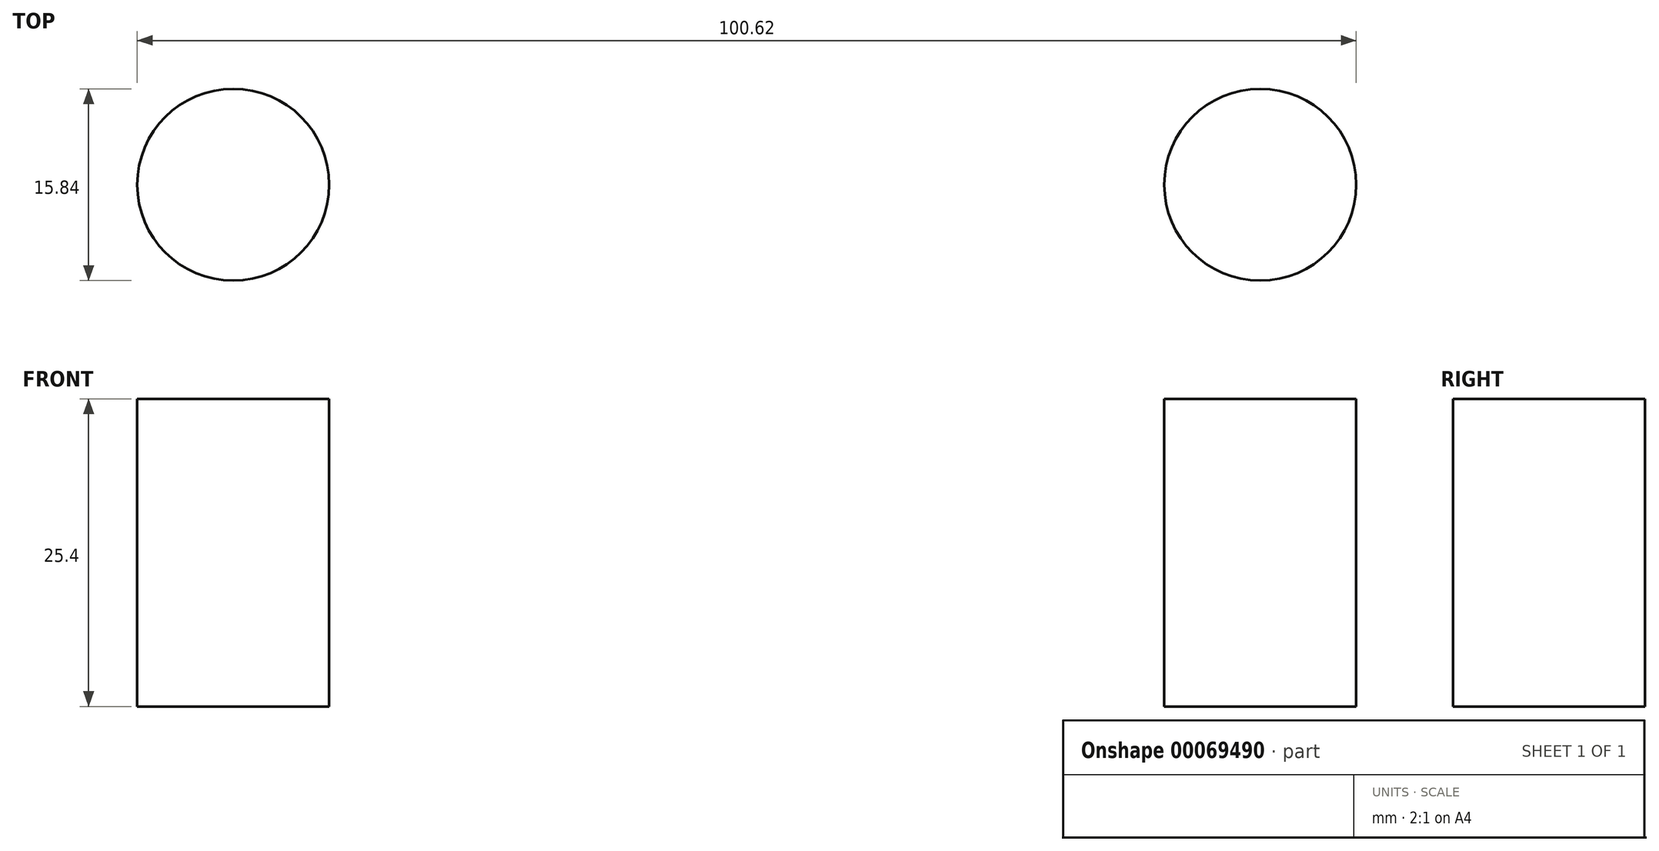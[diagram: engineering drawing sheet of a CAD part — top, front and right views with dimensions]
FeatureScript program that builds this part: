
annotation { "Feature Type Name" : "Feature", "Feature Type Description" : "" }
export const myFeature = defineFeature(function(context is Context, id is Id, definition is map)
    precondition{}
    {
        {
            var Q0;
            Q0=qCreatedBy(makeId("Top.planeOp"),FACE);
            var sketch = newSketch(context, id + "F0", { "sketchPlane" : qUnion([Q0])});
            skCircle(sketch, "E0", {"center": v(-42.38, 27.52) * mm, "radius": 7.92 * mm});
            skCircle(sketch, "E1.MirrorC", {"center": v(42.38, 27.52) * mm, "radius": 7.92 * mm});
            skSolve(sketch);
        }
        {
            var Q0;
            Q0 = qSketchRegion(id + "F0", true);
            extrude(context, id + "F1", {"entities" : qUnion([Q0]), "depth" : 25.4 * mm});
        }
    });
